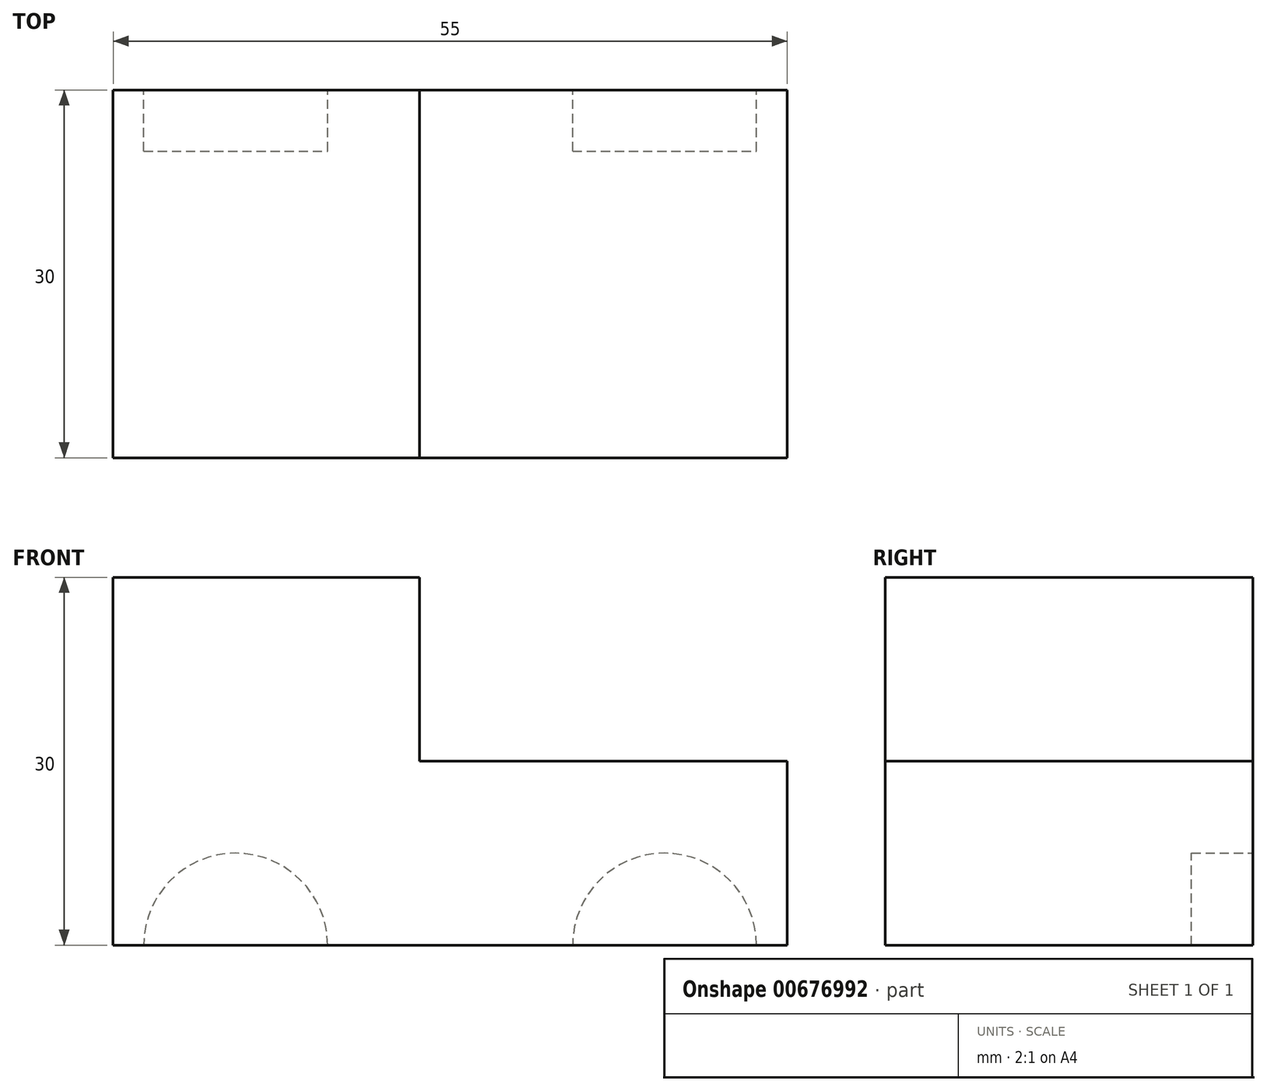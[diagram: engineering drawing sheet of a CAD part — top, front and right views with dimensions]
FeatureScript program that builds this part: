
annotation { "Feature Type Name" : "Feature", "Feature Type Description" : "" }
export const myFeature = defineFeature(function(context is Context, id is Id, definition is map)
    precondition{}
    {
        {
            var Q0;
            Q0=qCreatedBy(makeId("Top.planeOp"),FACE);
            var sketch = newSketch(context, id + "F0", { "sketchPlane" : qUnion([Q0])});
            skLineSegment(sketch, "E0.bottom", {"start": v(-18.4, 24.91) * mm, "end": v(36.6, 24.91) * mm});
            skLineSegment(sketch, "E0.top", {"start": v(-18.4, -5.09) * mm, "end": v(36.6, -5.09) * mm});
            skLineSegment(sketch, "E0.left", {"start": v(-18.4, 24.91) * mm, "end": v(-18.4, -5.09) * mm});
            skLineSegment(sketch, "E0.right", {"start": v(36.6, 24.91) * mm, "end": v(36.6, -5.09) * mm});
            skSolve(sketch);
        }
        {
            var Q0;
            Q0=makeQuery(id+"F0.imprint","IMPRINT",FACE,{"disambiguationData":[TD([[makeQuery(id+"F0.imprint","IMPRINT",EDGE,{"derivedFrom":sQuery(id+"F0.wireOp",EDGE,"E0.bottom")}),-1.0]])]});
            extrude(context, id + "F1", {"entities" : qUnion([Q0]), "depth" : 30 * mm, "offsetDistance" : 25 * mm});
        }
        {
            var Q0;
            Q0=makeQuery(id+"F1.opExtrude","SWEPT_FACE",FACE,{"disambiguationData":[OSD([sQuery(id+"F0.wireOp",EDGE,"E0.bottom")])]});
            var sketch = newSketch(context, id + "F2", { "sketchPlane" : qUnion([Q0])});
            skLineSegment(sketch, "E1", {"start": v(-36.6, 15) * mm, "end": v(-6.6, 15) * mm});
            skLineSegment(sketch, "E2", {"start": v(-6.6, 30) * mm, "end": v(-6.6, 15) * mm});
            skLineSegment(sketch, "E3", {"start": v(-6.6, 30) * mm, "end": v(18.4, 30) * mm});
            skSolve(sketch);
        }
        {
            var Q0;
            Q0 = qSketchRegion(id + "F2", true);
            var Q1;
            {var subQ0=sQuery(id+"F2.wireOp",EDGE,"E1");Q1=makeQuery(id+"F2.imprint","IMPRINT",FACE,{"disambiguationData":[TD([[makeQuery(id+"F2.imprint","IMPRINT",EDGE,{"derivedFrom":subQ0}),1.0]])]});}
            extrude(context, id + "F3", {"entities" : qUnion([Q0, Q1]), "operationType" : NewBodyOperationType.REMOVE, "endBound" : BoundingType.THROUGH_ALL, "oppositeDirection" : true, "depth" : 25 * mm, "offsetDistance" : 25 * mm});
        }
        {
            var Q0;
            Q0=makeQuery(id+"F1.opExtrude","SWEPT_FACE",FACE,{"disambiguationData":[OSD([sQuery(id+"F0.wireOp",EDGE,"E0.bottom")])]});
            var sketch = newSketch(context, id + "F4", { "sketchPlane" : qUnion([Q0])});
            skCircle(sketch, "E4", {"center": v(-26.6, 0) * mm, "radius": 7.5 * mm});
            skCircle(sketch, "E5.1.0.0", {"center": v(8.4, 0) * mm, "radius": 7.5 * mm});
            skLineSegment(sketch, "E5.direction1", {"start": v(-26.6, 0) * mm, "end": v(8.4, 0) * mm, "construction": true});
            skSolve(sketch);
        }
        {
            var Q0;
            {var subQ0=sQuery(id+"F4.wireOp",EDGE,"E4");var subQ1=makeQuery(id+"F1.opExtrude","CAP_EDGE",EDGE,{"disambiguationData":[OSD([sQuery(id+"F0.wireOp",EDGE,"E0.bottom")])],"isStart":true});var subQ2=makeQuery(id+"F4.imprint","INTERSECT",VERTEX,{"disambiguationData":[OD(0.0)],"derivedFrom":[subQ1,subQ0]});Q0=makeQuery(id+"F4.imprint","IMPRINT",FACE,{"disambiguationData":[TD([[makeQuery(id+"F4.imprint","IMPRINT",EDGE,{"disambiguationData":[TD([[subQ2,1.0]])],"derivedFrom":subQ0}),1.0]])]});}
            var Q1;
            {var subQ0=sQuery(id+"F4.wireOp",EDGE,"E5.1.0.0");var subQ1=makeQuery(id+"F1.opExtrude","CAP_EDGE",EDGE,{"disambiguationData":[OSD([sQuery(id+"F0.wireOp",EDGE,"E0.bottom")])],"isStart":true});var subQ2=makeQuery(id+"F4.imprint","INTERSECT",VERTEX,{"disambiguationData":[OD(0.0)],"derivedFrom":[subQ1,subQ0]});Q1=makeQuery(id+"F4.imprint","IMPRINT",FACE,{"disambiguationData":[TD([[makeQuery(id+"F4.imprint","IMPRINT",EDGE,{"disambiguationData":[TD([[subQ2,-1.0]])],"derivedFrom":subQ0}),1.0]])]});}
            extrude(context, id + "F5", {"entities" : qUnion([Q0, Q1]), "operationType" : NewBodyOperationType.REMOVE, "oppositeDirection" : true, "depth" : 5 * mm, "offsetDistance" : 25 * mm});
        }
    });
